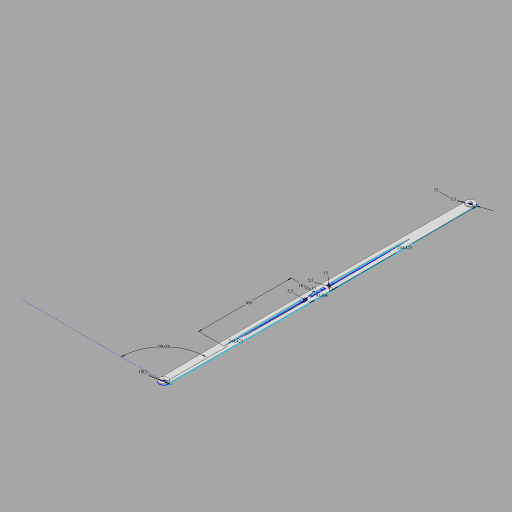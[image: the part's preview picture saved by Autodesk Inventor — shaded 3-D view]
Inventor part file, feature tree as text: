
AUTODESK INVENTOR PART (.ipt)
format: ipt  version: 2023 (Build 270158000, 158)  size: 135,168 bytes
history: native  units: mm
features: extrude x3, sketch x1
ambient origin geometry x8: Origin, YZ Plane, XZ Plane, XY Plane, X Axis, Y Axis, Z Axis, Center Point
bodies: Solid1 (feature_tree)
feature tree (4):
  sketch  "Sketch1"  dims[d0=244.423mm d1=90.0deg d2=41.005864mm d3=244.423mm d4=5.5mm d5=5.5mm d6=5.5mm d7=15.0mm d8=15.0mm d9=18.0mm d10=5.5mm d11=2.0mm d12=0.0mm d13=1.0mm d14=0.0mm d15=160.0mm d16=15.0mm d17=15.0mm d18=1.0mm d19=0.0mm]
  extrude  "Extrusion1"  TaperAngle=90.0deg  [1 undecoded]
  extrude  "Extrusion2"  Depth=1.0mm
  extrude  "Extrusion3"  Depth=244.423mm
note: 1 required parameter value undecoded (feature->parameter linkage not recoverable at this tier; creation-order binding heuristic only, values carry confidence <= 0.55)
